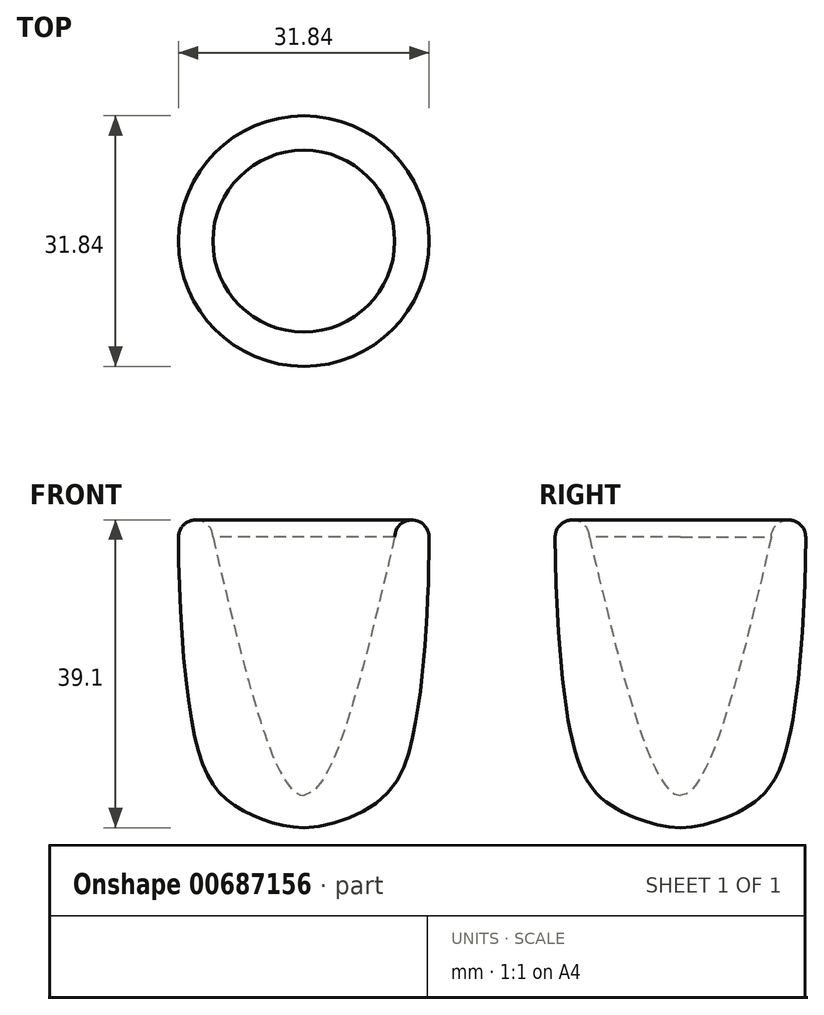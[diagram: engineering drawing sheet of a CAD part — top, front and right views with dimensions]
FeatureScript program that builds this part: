
annotation { "Feature Type Name" : "Feature", "Feature Type Description" : "" }
export const myFeature = defineFeature(function(context is Context, id is Id, definition is map)
    precondition{}
    {
        {
            var Q0;
            Q0=qCreatedBy(makeId("Front.planeOp"),FACE);
            var sketch = newSketch(context, id + "F0", { "sketchPlane" : qUnion([Q0])});
            skLineSegment(sketch, "E0", {"start": v(0, 0) * mm, "end": v(0, 36.92) * mm, "construction": true});
            skFitSpline(sketch, "E1", {"points": [v(15.92, 36.92) * mm, v(13.73, 11.07) * mm, v(10.5, 4.23) * mm, v(5.75, 1.28) * mm, v(0, 0) * mm, v(-5.75, 1.28) * mm, v(-10.5, 4.23) * mm, v(-13.73, 11.07) * mm, v(-15.92, 36.92) * mm], "startDerivative": vector(-6.66, -146.97) * mm, "endDerivative": vector(-0.35, 141.29) * mm});
            skLineSegment(sketch, "E2", {"start": v(13.73, 11.07) * mm, "end": v(13.73, 0) * mm, "construction": true});
            skLineSegment(sketch, "E3", {"start": v(10.5, 4.23) * mm, "end": v(10.5, 0) * mm, "construction": true});
            skLineSegment(sketch, "E4", {"start": v(5.75, 1.28) * mm, "end": v(5.75, 0) * mm, "construction": true});
            skLineSegment(sketch, "E5", {"start": v(-5.75, 1.28) * mm, "end": v(-5.75, 0) * mm, "construction": true});
            skLineSegment(sketch, "E6", {"start": v(-10.5, 4.23) * mm, "end": v(-10.5, 0) * mm, "construction": true});
            skLineSegment(sketch, "E7", {"start": v(-13.73, 11.07) * mm, "end": v(-13.73, 0) * mm, "construction": true});
            skLineSegment(sketch, "E8", {"start": v(-15.92, 36.92) * mm, "end": v(-11.55, 36.92) * mm, "construction": true});
            skLineSegment(sketch, "E9", {"start": v(-11.55, 36.92) * mm, "end": v(0, 36.92) * mm, "construction": true});
            skLineSegment(sketch, "E10", {"start": v(11.55, 36.92) * mm, "end": v(15.92, 36.92) * mm, "construction": true});
            skLineSegment(sketch, "E11", {"start": v(11.55, 36.92) * mm, "end": v(0, 36.92) * mm, "construction": true});
            skLineSegment(sketch, "E12", {"start": v(15.92, 36.92) * mm, "end": v(15.92, 0) * mm, "construction": true});
            skLineSegment(sketch, "E13", {"start": v(15.92, 0) * mm, "end": v(13.73, 0) * mm, "construction": true});
            skLineSegment(sketch, "E14", {"start": v(10.5, 0) * mm, "end": v(5.75, 0) * mm, "construction": true});
            skLineSegment(sketch, "E15", {"start": v(0, 0) * mm, "end": v(5.75, 0) * mm, "construction": true});
            skLineSegment(sketch, "E16", {"start": v(10.5, 0) * mm, "end": v(13.73, 0) * mm, "construction": true});
            skLineSegment(sketch, "E17", {"start": v(0, 0) * mm, "end": v(-5.75, 0) * mm, "construction": true});
            skLineSegment(sketch, "E18", {"start": v(-5.75, 0) * mm, "end": v(-10.5, 0) * mm, "construction": true});
            skLineSegment(sketch, "E19", {"start": v(-13.73, 0) * mm, "end": v(-10.5, 0) * mm, "construction": true});
            skLineSegment(sketch, "E20", {"start": v(-15.92, 36.92) * mm, "end": v(-15.92, 0) * mm, "construction": true});
            skLineSegment(sketch, "E21", {"start": v(-15.92, 0) * mm, "end": v(-13.73, 0) * mm, "construction": true});
            skArc(sketch, "E22", {"start": v(-11.55, 36.92) * mm, "mid": v(-13.73, 39.1) * mm, "end": v(-15.92, 36.92) * mm});
            skArc(sketch, "E23", {"start": v(15.92, 36.92) * mm, "mid": v(13.73, 39.1) * mm, "end": v(11.55, 36.92) * mm});
            skFitSpline(sketch, "E24", {"points": [v(-11.55, 36.92) * mm, v(0, 4.07) * mm, v(11.55, 36.92) * mm], "startDerivative": vector(23.1, -98.53) * mm, "endDerivative": vector(23.1, 98.53) * mm});
            skLineSegment(sketch, "E25", {"start": v(0, 4.07) * mm, "end": v(0, 0) * mm});
            skSolve(sketch);
        }
        {
            var Q0;
            {var subQ0=sQuery(id+"F0.wireOp",EDGE,"E22");Q0=makeQuery(id+"F0.imprint","IMPRINT",FACE,{"disambiguationData":[TD([[makeQuery(id+"F0.imprint","IMPRINT",EDGE,{"derivedFrom":subQ0}),1.0]])]});}
            var Q1;
            Q1=sQuery(id+"F0.wireOp",EDGE,"E0");
            revolve(context, id + "F1", {"entities" : qUnion([Q0]), "axis" : qUnion([Q1]), "revolveType" : RevolveType.FULL, "oppositeDirection" : true});
        }
    });
